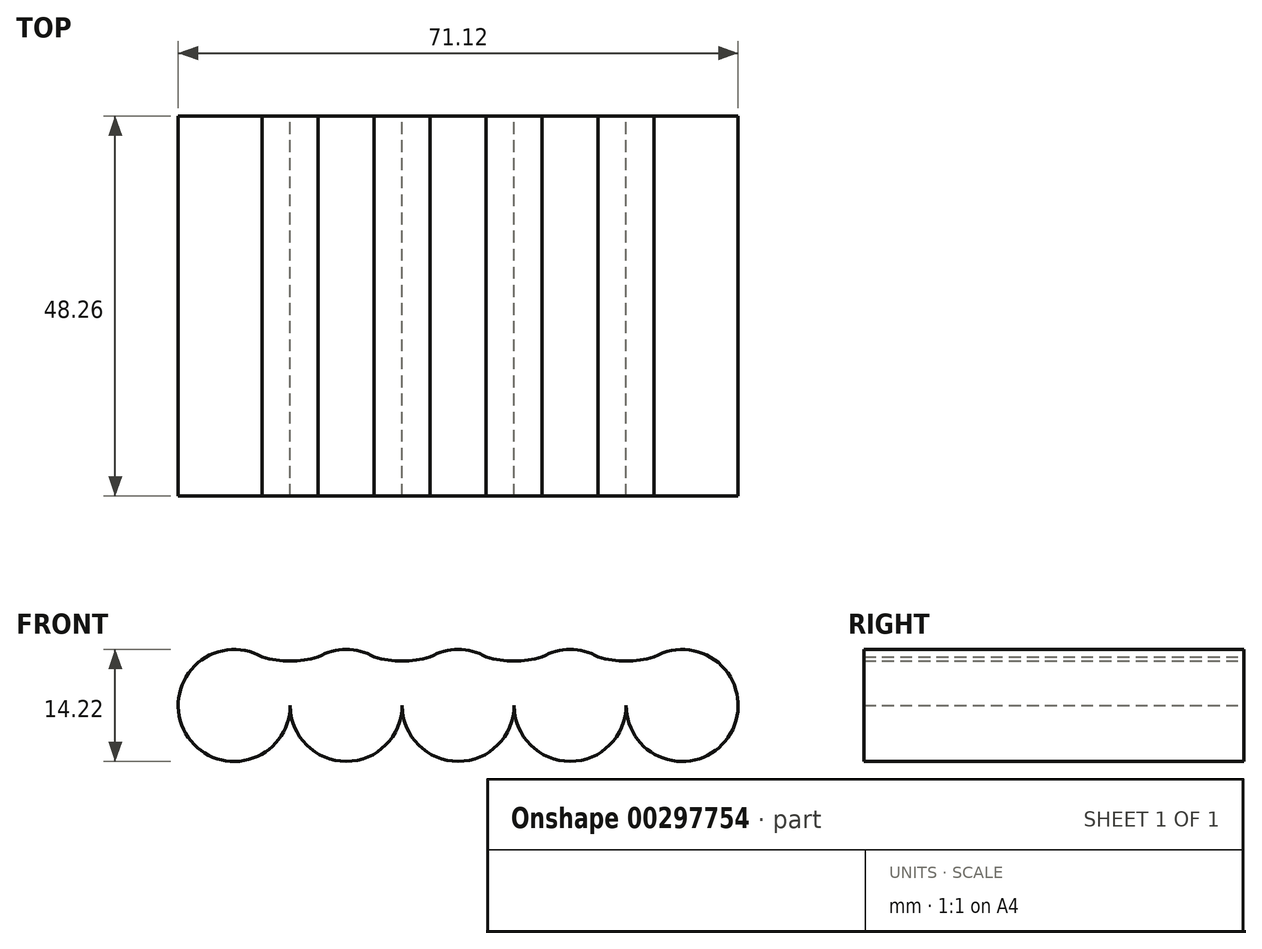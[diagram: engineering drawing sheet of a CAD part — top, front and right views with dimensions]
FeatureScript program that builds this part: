
annotation { "Feature Type Name" : "Feature", "Feature Type Description" : "" }
export const myFeature = defineFeature(function(context is Context, id is Id, definition is map)
    precondition{}
    {
        {
            var Q0;
            Q0=qCreatedBy(makeId("Front.planeOp"),FACE);
            var sketch = newSketch(context, id + "F0", { "sketchPlane" : qUnion([Q0])});
            skCircle(sketch, "E0", {"center": v(0, 0) * mm, "radius": 7.11 * mm});
            skCircle(sketch, "E1.1.0.0", {"center": v(-14.22, 0) * mm, "radius": 7.11 * mm});
            skCircle(sketch, "E1.2.0.0", {"center": v(-28.45, 0) * mm, "radius": 7.11 * mm});
            skLineSegment(sketch, "E1.direction1", {"start": v(-14.22, 0) * mm, "end": v(0, 0) * mm, "construction": true});
            skCircle(sketch, "E2.1.0.0", {"center": v(14.22, 0) * mm, "radius": 7.11 * mm});
            skCircle(sketch, "E2.2.0.0", {"center": v(28.45, 0) * mm, "radius": 7.11 * mm});
            skLineSegment(sketch, "E2.direction1", {"start": v(0, 0) * mm, "end": v(14.22, 0) * mm, "construction": true});
            skLineSegment(sketch, "E3", {"start": v(-28.45, 0) * mm, "end": v(-21.34, 0) * mm, "construction": true});
            skLineSegment(sketch, "E4", {"start": v(-24.9, 0) * mm, "end": v(-24.9, 6.16) * mm, "construction": true});
            skLineSegment(sketch, "E5", {"start": v(-14.22, 0) * mm, "end": v(-21.34, 0) * mm, "construction": true});
            skLineSegment(sketch, "E6", {"start": v(-17.78, 0) * mm, "end": v(-17.78, 6.16) * mm, "construction": true});
            skArc(sketch, "E7", {"start": v(-24.9, 6.16) * mm, "mid": v(-21.34, 5.65) * mm, "end": v(-17.78, 6.16) * mm});
            skArc(sketch, "E8.MirrorCS", {"start": v(-24.9, -6.16) * mm, "mid": v(-21.34, -5.65) * mm, "end": v(-17.78, -6.16) * mm});
            skArc(sketch, "E9.1.0.0", {"start": v(-10.67, 6.16) * mm, "mid": v(-7.11, 5.65) * mm, "end": v(-3.56, 6.16) * mm});
            skArc(sketch, "E9.2.0.0", {"start": v(3.56, 6.16) * mm, "mid": v(7.11, 5.65) * mm, "end": v(10.67, 6.16) * mm});
            skArc(sketch, "E9.3.0.0", {"start": v(17.78, 6.16) * mm, "mid": v(21.34, 5.65) * mm, "end": v(24.9, 6.16) * mm});
            skLineSegment(sketch, "E9.direction1", {"start": v(-24.9, 6.16) * mm, "end": v(-10.67, 6.16) * mm, "construction": true});
            skArc(sketch, "E10.1.0.0", {"start": v(-10.67, -6.16) * mm, "mid": v(-7.11, -5.65) * mm, "end": v(-3.56, -6.16) * mm});
            skArc(sketch, "E10.2.0.0", {"start": v(3.56, -6.16) * mm, "mid": v(7.11, -5.65) * mm, "end": v(10.67, -6.16) * mm});
            skArc(sketch, "E10.3.0.0", {"start": v(17.78, -6.16) * mm, "mid": v(21.34, -5.65) * mm, "end": v(24.9, -6.16) * mm});
            skLineSegment(sketch, "E10.direction1", {"start": v(-21.34, -18.37) * mm, "end": v(-7.11, -18.37) * mm, "construction": true});
            skSolve(sketch);
        }
        {
            var Q0;
            {var subQ0=sQuery(id+"F0.wireOp",EDGE,"E0");var subQ1=makeQuery(id+"F0.imprint","INTERSECT",VERTEX,{"derivedFrom":[subQ0,sQuery(id+"F0.wireOp",EDGE,"E1.1.0.0")]});Q0=makeQuery(id+"F0.imprint","IMPRINT",FACE,{"disambiguationData":[TD([[makeQuery(id+"F0.imprint","IMPRINT",EDGE,{"disambiguationData":[TD([[subQ1,1.0]])],"derivedFrom":subQ0}),1.0]])]});}
            var Q1;
            {var subQ0=sQuery(id+"F0.wireOp",EDGE,"E1.1.0.0");var subQ1=makeQuery(id+"F0.imprint","INTERSECT",VERTEX,{"derivedFrom":[sQuery(id+"F0.wireOp",EDGE,"E0"),subQ0]});Q1=makeQuery(id+"F0.imprint","IMPRINT",FACE,{"disambiguationData":[TD([[makeQuery(id+"F0.imprint","IMPRINT",EDGE,{"disambiguationData":[TD([[subQ1,-1.0]])],"derivedFrom":subQ0}),1.0]])]});}
            var Q2;
            Q2=makeQuery(id+"F0.imprint","IMPRINT",FACE,{"disambiguationData":[TD([[makeQuery(id+"F0.imprint","IMPRINT",EDGE,{"derivedFrom":sQuery(id+"F0.wireOp",EDGE,"E1.2.0.0")}),1.0]])]});
            var Q3;
            {var subQ0=sQuery(id+"F0.wireOp",EDGE,"E2.1.0.0");var subQ1=makeQuery(id+"F0.imprint","INTERSECT",VERTEX,{"derivedFrom":[sQuery(id+"F0.wireOp",EDGE,"E0"),subQ0]});Q3=makeQuery(id+"F0.imprint","IMPRINT",FACE,{"disambiguationData":[TD([[makeQuery(id+"F0.imprint","IMPRINT",EDGE,{"disambiguationData":[TD([[subQ1,1.0]])],"derivedFrom":subQ0}),1.0]])]});}
            var Q4;
            Q4=makeQuery(id+"F0.imprint","IMPRINT",FACE,{"disambiguationData":[TD([[makeQuery(id+"F0.imprint","IMPRINT",EDGE,{"derivedFrom":sQuery(id+"F0.wireOp",EDGE,"E2.2.0.0")}),1.0]])]});
            var Q5;
            {var subQ0=sQuery(id+"F0.wireOp",EDGE,"5ab4537a-ec12-4f53-b692-81b737fed133");Q5=makeQuery(id+"F0.imprint","IMPRINT",FACE,{"disambiguationData":[TD([[makeQuery(id+"F0.imprint","IMPRINT",EDGE,{"derivedFrom":subQ0}),-1.0]])]});}
            var Q6;
            {var subQ0=sQuery(id+"F0.wireOp",EDGE,"e9c96bc6-f74b-4f4f-a07e-e48e70047498.1.0.0");Q6=makeQuery(id+"F0.imprint","IMPRINT",FACE,{"disambiguationData":[TD([[makeQuery(id+"F0.imprint","IMPRINT",EDGE,{"derivedFrom":subQ0}),-1.0]])]});}
            var Q7;
            {var subQ0=sQuery(id+"F0.wireOp",EDGE,"e9c96bc6-f74b-4f4f-a07e-e48e70047498.2.0.0");Q7=makeQuery(id+"F0.imprint","IMPRINT",FACE,{"disambiguationData":[TD([[makeQuery(id+"F0.imprint","IMPRINT",EDGE,{"derivedFrom":subQ0}),-1.0]])]});}
            var Q8;
            {var subQ0=sQuery(id+"F0.wireOp",EDGE,"e9c96bc6-f74b-4f4f-a07e-e48e70047498.3.0.0");Q8=makeQuery(id+"F0.imprint","IMPRINT",FACE,{"disambiguationData":[TD([[makeQuery(id+"F0.imprint","IMPRINT",EDGE,{"derivedFrom":subQ0}),-1.0]])]});}
            var Q9;
            {var subQ0=sQuery(id+"F0.wireOp",EDGE,"e9c96bc6-f74b-4f4f-a07e-e48e70047498.3.0.1");Q9=makeQuery(id+"F0.imprint","IMPRINT",FACE,{"disambiguationData":[TD([[makeQuery(id+"F0.imprint","IMPRINT",EDGE,{"derivedFrom":subQ0}),1.0]])]});}
            var Q10;
            {var subQ0=sQuery(id+"F0.wireOp",EDGE,"e9c96bc6-f74b-4f4f-a07e-e48e70047498.2.0.1");Q10=makeQuery(id+"F0.imprint","IMPRINT",FACE,{"disambiguationData":[TD([[makeQuery(id+"F0.imprint","IMPRINT",EDGE,{"derivedFrom":subQ0}),1.0]])]});}
            var Q11;
            {var subQ0=sQuery(id+"F0.wireOp",EDGE,"e9c96bc6-f74b-4f4f-a07e-e48e70047498.1.0.1");Q11=makeQuery(id+"F0.imprint","IMPRINT",FACE,{"disambiguationData":[TD([[makeQuery(id+"F0.imprint","IMPRINT",EDGE,{"derivedFrom":subQ0}),1.0]])]});}
            var Q12;
            {var subQ0=sQuery(id+"F0.wireOp",EDGE,"b308b551-caff-4138-940b-d6c43c5917ac0.MirrorCS");Q12=makeQuery(id+"F0.imprint","IMPRINT",FACE,{"disambiguationData":[TD([[makeQuery(id+"F0.imprint","IMPRINT",EDGE,{"derivedFrom":subQ0}),1.0]])]});}
            var Q13;
            {var subQ0=sQuery(id+"F0.wireOp",EDGE,"E9.2.0.0");Q13=makeQuery(id+"F0.imprint","IMPRINT",FACE,{"disambiguationData":[TD([[makeQuery(id+"F0.imprint","IMPRINT",EDGE,{"derivedFrom":subQ0}),-1.0]])]});}
            var Q14;
            {var subQ0=sQuery(id+"F0.wireOp",EDGE,"E9.3.0.0");Q14=makeQuery(id+"F0.imprint","IMPRINT",FACE,{"disambiguationData":[TD([[makeQuery(id+"F0.imprint","IMPRINT",EDGE,{"derivedFrom":subQ0}),-1.0]])]});}
            var Q15;
            {var subQ0=sQuery(id+"F0.wireOp",EDGE,"E9.1.0.0");Q15=makeQuery(id+"F0.imprint","IMPRINT",FACE,{"disambiguationData":[TD([[makeQuery(id+"F0.imprint","IMPRINT",EDGE,{"derivedFrom":subQ0}),-1.0]])]});}
            var Q16;
            {var subQ0=sQuery(id+"F0.wireOp",EDGE,"E7");Q16=makeQuery(id+"F0.imprint","IMPRINT",FACE,{"disambiguationData":[TD([[makeQuery(id+"F0.imprint","IMPRINT",EDGE,{"derivedFrom":subQ0}),-1.0]])]});}
            var Q17;
            {var subQ0=sQuery(id+"F0.wireOp",EDGE,"E8.MirrorCS");Q17=makeQuery(id+"F0.imprint","IMPRINT",FACE,{"disambiguationData":[TD([[makeQuery(id+"F0.imprint","IMPRINT",EDGE,{"derivedFrom":subQ0}),1.0]])]});}
            var Q18;
            {var subQ0=sQuery(id+"F0.wireOp",EDGE,"E10.1.0.0");Q18=makeQuery(id+"F0.imprint","IMPRINT",FACE,{"disambiguationData":[TD([[makeQuery(id+"F0.imprint","IMPRINT",EDGE,{"derivedFrom":subQ0}),1.0]])]});}
            var Q19;
            {var subQ0=sQuery(id+"F0.wireOp",EDGE,"E10.2.0.0");Q19=makeQuery(id+"F0.imprint","IMPRINT",FACE,{"disambiguationData":[TD([[makeQuery(id+"F0.imprint","IMPRINT",EDGE,{"derivedFrom":subQ0}),1.0]])]});}
            var Q20;
            {var subQ0=sQuery(id+"F0.wireOp",EDGE,"E10.3.0.0");Q20=makeQuery(id+"F0.imprint","IMPRINT",FACE,{"disambiguationData":[TD([[makeQuery(id+"F0.imprint","IMPRINT",EDGE,{"derivedFrom":subQ0}),1.0]])]});}
            extrude(context, id + "F1", {"entities" : qUnion([Q0, Q1, Q2, Q3, Q4, Q5, Q6, Q7, Q8, Q9, Q10, Q11, Q12, Q13, Q14, Q15, Q16, Q17, Q18, Q19, Q20]), "depth" : 48.26 * mm});
        }
    });
